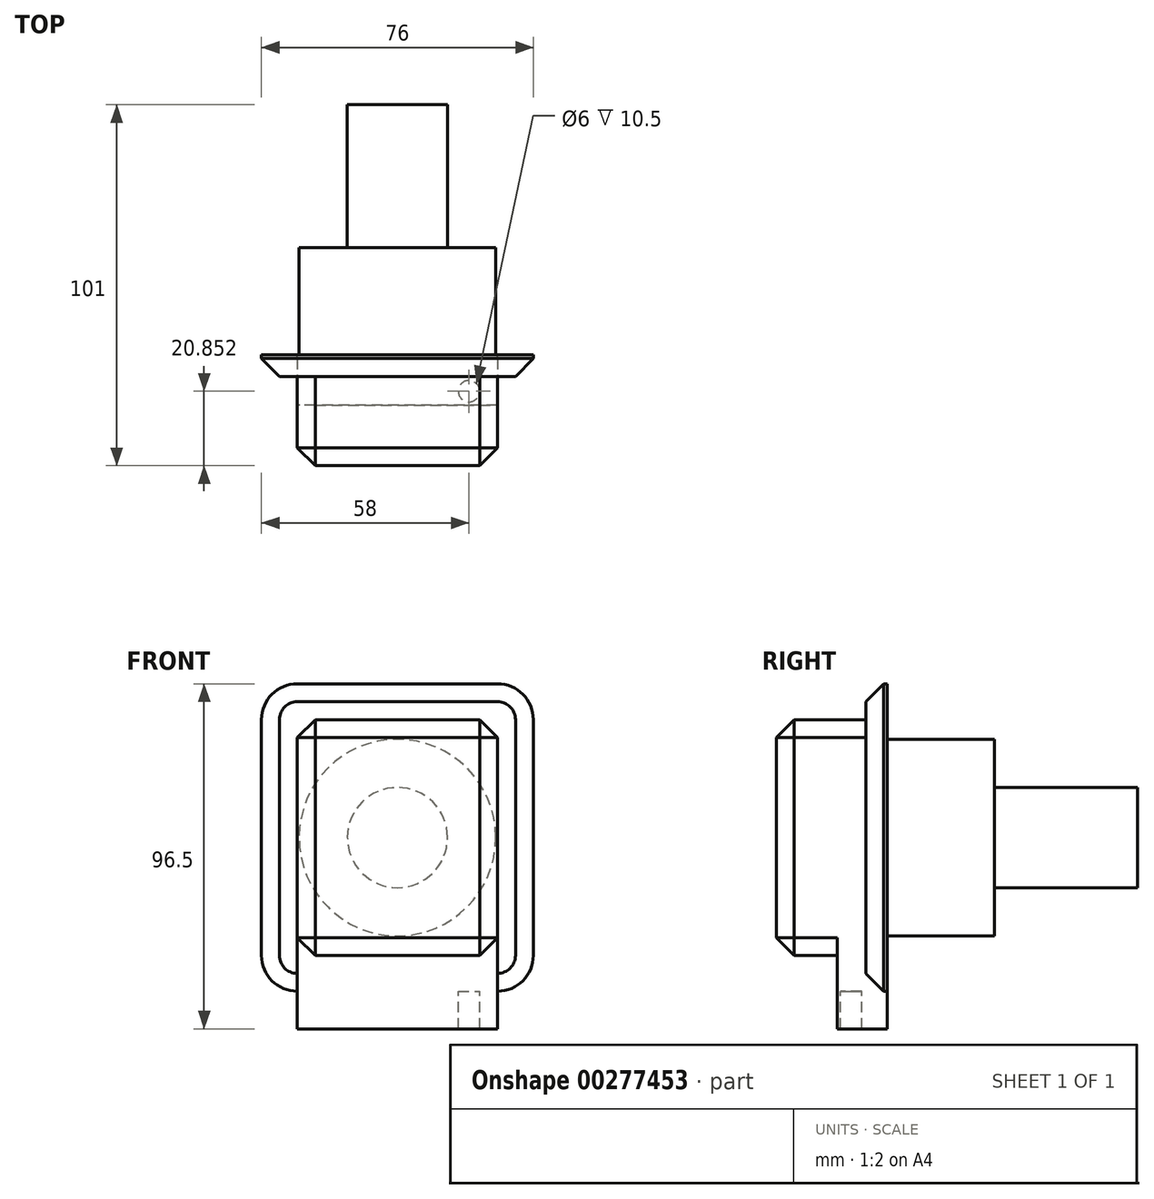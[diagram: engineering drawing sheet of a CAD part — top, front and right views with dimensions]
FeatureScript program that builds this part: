
annotation { "Feature Type Name" : "Feature", "Feature Type Description" : "" }
export const myFeature = defineFeature(function(context is Context, id is Id, definition is map)
    precondition{}
    {
        {
            var Q0;
            Q0=qCreatedBy(makeId("Front.planeOp"),FACE);
            var sketch = newSketch(context, id + "F0", { "sketchPlane" : qUnion([Q0])});
            skLineSegment(sketch, "E0.bottom", {"start": v(28, 43) * mm, "end": v(-28, 43) * mm});
            skLineSegment(sketch, "E0.top", {"start": v(28, -43) * mm, "end": v(-28, -43) * mm});
            skLineSegment(sketch, "E0.left", {"start": v(38, 33) * mm, "end": v(38, -33) * mm});
            skLineSegment(sketch, "E0.right", {"start": v(-38, 33) * mm, "end": v(-38, -33) * mm});
            skPoint(sketch, "E0.middle", {"position": v(0, 0) * mm});
            skPoint(sketch, "E1.visualSharp", {"position": v(-38, 43) * mm});
            skArc(sketch, "E1.filletArc", {"start": v(-28, 43) * mm, "mid": v(-35.07, 40.07) * mm, "end": v(-38, 33) * mm});
            skPoint(sketch, "E2.visualSharp", {"position": v(38, 43) * mm});
            skArc(sketch, "E2.filletArc", {"start": v(38, 33) * mm, "mid": v(35.07, 40.07) * mm, "end": v(28, 43) * mm});
            skPoint(sketch, "E3.visualSharp", {"position": v(38, -43) * mm});
            skArc(sketch, "E3.filletArc", {"start": v(28, -43) * mm, "mid": v(35.07, -40.07) * mm, "end": v(38, -33) * mm});
            skPoint(sketch, "E4.visualSharp", {"position": v(-38, -43) * mm});
            skArc(sketch, "E4.filletArc", {"start": v(-38, -33) * mm, "mid": v(-35.07, -40.07) * mm, "end": v(-28, -43) * mm});
            skSolve(sketch);
        }
        {
            var Q0;
            Q0 = qSketchRegion(id + "F0", true);
            extrude(context, id + "F1", {"entities" : qUnion([Q0]), "depth" : 6 * mm});
        }
        {
            var Q0;
            Q0=makeQuery(id+"F1.opExtrude","CAP_FACE",FACE,{"disambiguationData":[OSD([sQuery(id+"F0.wireOp",EDGE,"E0.bottom"),sQuery(id+"F0.wireOp",EDGE,"E0.top"),sQuery(id+"F0.wireOp",EDGE,"E0.left"),sQuery(id+"F0.wireOp",EDGE,"E0.right")])],"isStart":true});
            var sketch = newSketch(context, id + "F2", { "sketchPlane" : qUnion([Q0])});
            skCircle(sketch, "E5", {"center": v(0, 0) * mm, "radius": 27.5 * mm});
            skSolve(sketch);
        }
        {
            var Q0;
            Q0 = qSketchRegion(id + "F2", true);
            extrude(context, id + "F3", {"entities" : qUnion([Q0]), "operationType" : NewBodyOperationType.ADD, "depth" : 30 * mm});
        }
        {
            var Q0;
            Q0=makeQuery(id+"F3.opExtrude","CAP_FACE",FACE,{"disambiguationData":[OSD([sQuery(id+"F2.wireOp",EDGE,"E5")])],"isStart":false});
            var sketch = newSketch(context, id + "F4", { "sketchPlane" : qUnion([Q0])});
            skCircle(sketch, "E6", {"center": v(0, 0) * mm, "radius": 14 * mm});
            skSolve(sketch);
        }
        {
            var Q0;
            Q0=makeQuery(id+"F4.imprint","IMPRINT",FACE,{"disambiguationData":[TD([[makeQuery(id+"F4.imprint","IMPRINT",EDGE,{"derivedFrom":sQuery(id+"F4.wireOp",EDGE,"E6")}),1.0]])]});
            extrude(context, id + "F5", {"entities" : qUnion([Q0]), "operationType" : NewBodyOperationType.ADD, "depth" : 40 * mm});
        }
        {
            var Q0;
            Q0=makeQuery(id+"F1.opExtrude","CAP_FACE",FACE,{"disambiguationData":[OSD([sQuery(id+"F0.wireOp",EDGE,"E0.bottom"),sQuery(id+"F0.wireOp",EDGE,"E0.top"),sQuery(id+"F0.wireOp",EDGE,"E0.left"),sQuery(id+"F0.wireOp",EDGE,"E0.right"),sQuery(id+"F0.wireOp",EDGE,"E1.filletArc"),sQuery(id+"F0.wireOp",EDGE,"E2.filletArc"),sQuery(id+"F0.wireOp",EDGE,"E3.filletArc"),sQuery(id+"F0.wireOp",EDGE,"E4.filletArc")])],"isStart":false});
            var sketch = newSketch(context, id + "F6", { "sketchPlane" : qUnion([Q0])});
            skPoint(sketch, "E7.0", {"position": v(-28, -43) * mm});
            skLineSegment(sketch, "E8.bottom", {"start": v(-28, -43) * mm, "end": v(28, -43) * mm});
            skLineSegment(sketch, "E8.top", {"start": v(-28, -33) * mm, "end": v(28, -33) * mm});
            skLineSegment(sketch, "E8.left", {"start": v(-28, -43) * mm, "end": v(-28, -33) * mm});
            skLineSegment(sketch, "E8.right", {"start": v(28, -43) * mm, "end": v(28, -33) * mm});
            skSolve(sketch);
        }
        {
            var Q0;
            Q0 = qSketchRegion(id + "F6", true);
            extrude(context, id + "F7", {"entities" : qUnion([Q0]), "operationType" : NewBodyOperationType.ADD, "depth" : 8 * mm});
        }
        {
            var Q0;
            Q0=makeQuery(id+"F7.boolean.opBoolean","MERGE",FACE,{"derivedFrom":[makeQuery(id+"F1.opExtrude","SWEPT_FACE",FACE,{"disambiguationData":[OSD([sQuery(id+"F0.wireOp",EDGE,"E0.top")])]}),makeQuery(id+"F7.opExtrude","SWEPT_FACE",FACE,{"disambiguationData":[OSD([sQuery(id+"F6.wireOp",EDGE,"E8.bottom")])]})]});
            var sketch = newSketch(context, id + "F8", { "sketchPlane" : qUnion([Q0])});
            skCircle(sketch, "E9", {"center": v(-20, 10.15) * mm, "radius": 3 * mm});
            skCircle(sketch, "E10.MirrorC", {"center": v(20, 10.15) * mm, "radius": 3 * mm});
            skSolve(sketch);
        }
        {
            var Q0;
            Q0=makeQuery(id+"F8.imprint","IMPRINT",FACE,{"disambiguationData":[TD([[makeQuery(id+"F8.imprint","IMPRINT",EDGE,{"derivedFrom":sQuery(id+"F8.wireOp",EDGE,"E9")}),1.0]])]});
            var Q1;
            Q1=makeQuery(id+"F8.imprint","IMPRINT",FACE,{"disambiguationData":[TD([[makeQuery(id+"F8.imprint","IMPRINT",EDGE,{"derivedFrom":sQuery(id+"F8.wireOp",EDGE,"E10.MirrorC")}),-1.0]])]});
            extrude(context, id + "F9", {"entities" : qUnion([Q0, Q1]), "operationType" : NewBodyOperationType.ADD, "depth" : 10.5 * mm});
        }
        {
            var Q0;
            Q0=makeQuery(id+"F1.opExtrude","CAP_FACE",FACE,{"disambiguationData":[OSD([sQuery(id+"F0.wireOp",EDGE,"E0.bottom"),sQuery(id+"F0.wireOp",EDGE,"E0.top"),sQuery(id+"F0.wireOp",EDGE,"E0.left"),sQuery(id+"F0.wireOp",EDGE,"E0.right"),sQuery(id+"F0.wireOp",EDGE,"E1.filletArc"),sQuery(id+"F0.wireOp",EDGE,"E2.filletArc"),sQuery(id+"F0.wireOp",EDGE,"E3.filletArc"),sQuery(id+"F0.wireOp",EDGE,"E4.filletArc")])],"isStart":false});
            var sketch = newSketch(context, id + "F10", { "sketchPlane" : qUnion([Q0])});
            skLineSegment(sketch, "E11.bottom", {"start": v(-28, 33) * mm, "end": v(28, 33) * mm});
            skLineSegment(sketch, "E11.top", {"start": v(-28, -33) * mm, "end": v(28, -33) * mm});
            skLineSegment(sketch, "E11.left", {"start": v(-28, 33) * mm, "end": v(-28, -33) * mm});
            skLineSegment(sketch, "E11.right", {"start": v(28, 33) * mm, "end": v(28, -33) * mm});
            skSolve(sketch);
        }
        {
            var Q0;
            Q0 = qSketchRegion(id + "F10", true);
            extrude(context, id + "F11", {"entities" : qUnion([Q0]), "operationType" : NewBodyOperationType.ADD, "depth" : 25 * mm});
        }
        {
            var Q0;
            Q0=makeQuery(id+"F11.opExtrude","CAP_EDGE",EDGE,{"disambiguationData":[OSD([sQuery(id+"F10.wireOp",EDGE,"E11.bottom")])],"isStart":false});
            var Q1;
            Q1=makeQuery(id+"F11.opExtrude","CAP_EDGE",EDGE,{"disambiguationData":[OSD([sQuery(id+"F10.wireOp",EDGE,"E11.right")])],"isStart":false});
            var Q2;
            Q2=makeQuery(id+"F11.opExtrude","CAP_EDGE",EDGE,{"disambiguationData":[OSD([sQuery(id+"F10.wireOp",EDGE,"E11.left")])],"isStart":false});
            var Q3;
            Q3=makeQuery(id+"F11.opExtrude","SWEPT_EDGE",EDGE,{"disambiguationData":[OSD([sQuery(id+"F10.wireOp",EDGE,"E11.bottom"),sQuery(id+"F10.wireOp",EDGE,"E11.left")])]});
            var Q4;
            Q4=makeQuery(id+"F11.opExtrude","SWEPT_EDGE",EDGE,{"disambiguationData":[OSD([sQuery(id+"F10.wireOp",EDGE,"E11.bottom"),sQuery(id+"F10.wireOp",EDGE,"E11.right")])]});
            var Q5;
            Q5=makeQuery(id+"F11.opExtrude","SWEPT_EDGE",EDGE,{"disambiguationData":[OSD([sQuery(id+"F6.wireOp",EDGE,"E8.right"),sQuery(id+"F10.wireOp",EDGE,"E11.top"),sQuery(id+"F10.wireOp",EDGE,"E11.right")])]});
            var Q6;
            Q6=makeQuery(id+"F11.opExtrude","CAP_EDGE",EDGE,{"disambiguationData":[OSD([sQuery(id+"F10.wireOp",EDGE,"E11.top")])],"isStart":false});
            var Q7;
            Q7=makeQuery(id+"F11.opExtrude","SWEPT_EDGE",EDGE,{"disambiguationData":[OSD([sQuery(id+"F6.wireOp",EDGE,"E8.left"),sQuery(id+"F10.wireOp",EDGE,"E11.top"),sQuery(id+"F10.wireOp",EDGE,"E11.left")])]});
            var Q8;
            Q8=makeQuery(id+"F1.opExtrude","CAP_EDGE",EDGE,{"disambiguationData":[OSD([sQuery(id+"F0.wireOp",EDGE,"E0.bottom")])],"isStart":false});
            chamfer(context, id + "F12", {"entities" : qUnion([Q0, Q1, Q2, Q3, Q4, Q5, Q6, Q7, Q8]), "width" : 5 * mm, "tangentPropagation" : true});
        }
    });
